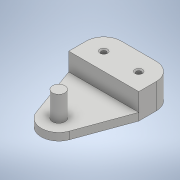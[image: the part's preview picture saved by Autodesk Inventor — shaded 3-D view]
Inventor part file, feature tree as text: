
AUTODESK INVENTOR PART (.ipt)
format: ipt  version: 2020 (Build 240168000, 168)  size: 142,336 bytes
history: native  units: mm
features: sketch x4, extrude x3, other x1, fillet x1, hole x1
ambient origin geometry x8: Origin, YZ Plane, XZ Plane, XY Plane, X Axis, Y Axis, Z Axis, Center Point
bodies: Body1 (feature_tree)
feature tree (10):
  other  "Твердое тело1"
  extrude  "Выдавливание1"  Depth=14.0mm
  extrude  "Выдавливание6"  Depth=7.0mm
  extrude  "Выдавливание9"  Depth=9.0mm
  fillet  "Сопряжение1"  Radius=3.5mm
  hole  "Отверстие1"  [1 undecoded]
  sketch  "Эскиз1"
  sketch  "Эскиз2"
  sketch  "Эскиз4"
  sketch  "Эскиз5"
note: 1 required parameter value undecoded (feature->parameter linkage not recoverable at this tier; creation-order binding heuristic only, values carry confidence <= 0.55)
